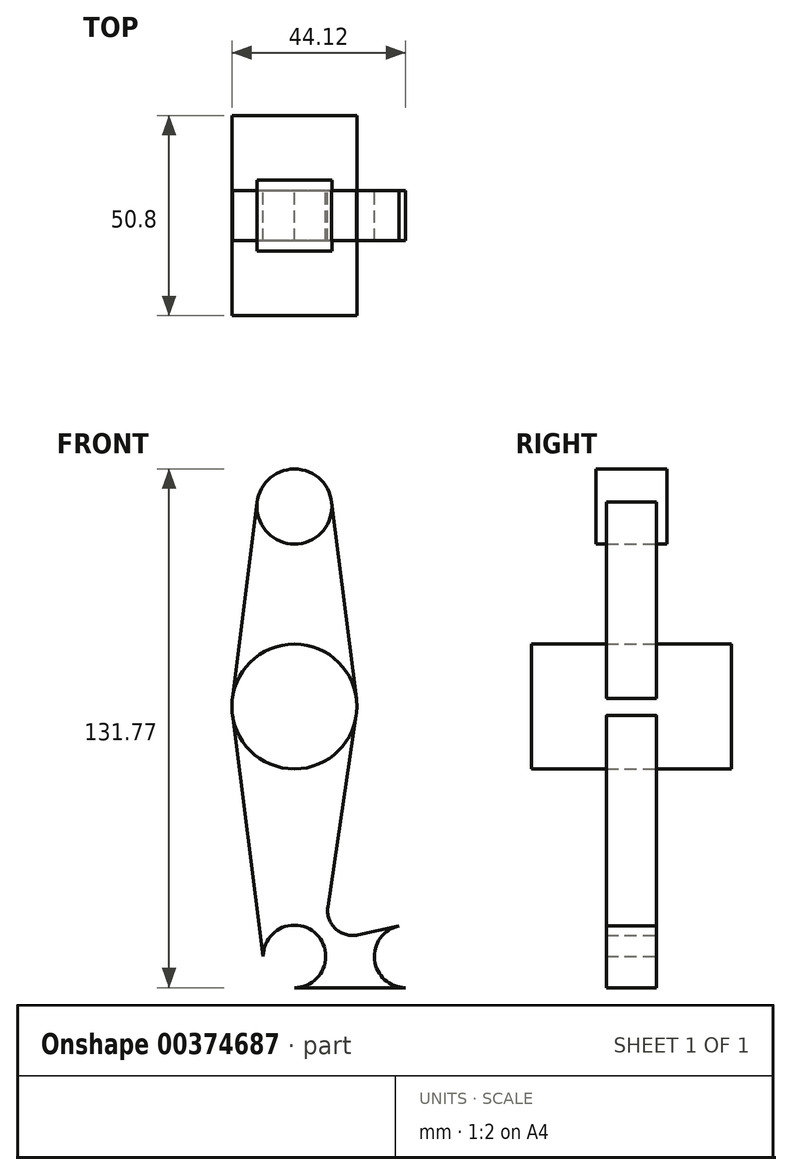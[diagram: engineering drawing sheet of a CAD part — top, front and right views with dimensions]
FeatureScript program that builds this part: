
annotation { "Feature Type Name" : "Feature", "Feature Type Description" : "" }
export const myFeature = defineFeature(function(context is Context, id is Id, definition is map)
    precondition{}
    {
        {
            var Q0;
            Q0=qCreatedBy(makeId("Front.planeOp"),FACE);
            var sketch = newSketch(context, id + "F0", { "sketchPlane" : qUnion([Q0])});
            skCircle(sketch, "E0", {"center": v(0, 0) * mm, "radius": 7.94 * mm});
            skCircle(sketch, "E1", {"center": v(0, 63.5) * mm, "radius": 15.88 * mm});
            skCircle(sketch, "E2", {"center": v(0, 114.3) * mm, "radius": 9.53 * mm});
            skCircle(sketch, "E3", {"center": v(28.24, 0) * mm, "radius": 7.94 * mm});
            skLineSegment(sketch, "E4", {"start": v(-9.45, 115.5) * mm, "end": v(-15.75, 65.48) * mm});
            skLineSegment(sketch, "E5", {"start": v(-7.94, 0) * mm, "end": v(-15.75, 61.5) * mm});
            skLineSegment(sketch, "E6", {"start": v(9.45, 115.5) * mm, "end": v(15.75, 65.48) * mm});
            skLineSegment(sketch, "E7", {"start": v(8.48, 12.6) * mm, "end": v(15.7, 61.16) * mm});
            skLineSegment(sketch, "E8", {"start": v(16.12, 5.47) * mm, "end": v(26.54, 7.75) * mm});
            skLineSegment(sketch, "E9", {"start": v(0, -7.94) * mm, "end": v(28.24, -7.94) * mm});
            skPoint(sketch, "E10.visualSharp", {"position": v(7.12, 3.5) * mm});
            skArc(sketch, "E10.filletArc", {"start": v(8.48, 12.6) * mm, "mid": v(10.42, 7.03) * mm, "end": v(16.12, 5.47) * mm});
            skLineSegment(sketch, "E11", {"start": v(-83.82, 96.93) * mm, "end": v(-83.82, 0) * mm, "construction": true});
            skSolve(sketch);
        }
        {
            var Q0;
            {var subQ0=sQuery(id+"F0.wireOp",EDGE,"E2");var subQ1=makeQuery(id+"F0.imprint","INTERSECT",VERTEX,{"derivedFrom":[subQ0,sQuery(id+"F0.wireOp",EDGE,"E4")]});Q0=makeQuery(id+"F0.imprint","IMPRINT",FACE,{"disambiguationData":[TD([[makeQuery(id+"F0.imprint","IMPRINT",EDGE,{"disambiguationData":[TD([[subQ1,1.0]])],"derivedFrom":subQ0}),1.0]])]});}
            extrude(context, id + "F1", {"entities" : qUnion([Q0]), "endBound" : BoundingType.SYMMETRIC, "depth" : 18.03 * mm});
        }
        {
            var Q0;
            {var subQ0=sQuery(id+"F0.wireOp",EDGE,"E1");var subQ1=makeQuery(id+"F0.imprint","INTERSECT",VERTEX,{"derivedFrom":[subQ0,sQuery(id+"F0.wireOp",EDGE,"E4")]});Q0=makeQuery(id+"F0.imprint","IMPRINT",FACE,{"disambiguationData":[TD([[makeQuery(id+"F0.imprint","IMPRINT",EDGE,{"disambiguationData":[TD([[subQ1,1.0]])],"derivedFrom":subQ0}),1.0]])]});}
            extrude(context, id + "F2", {"entities" : qUnion([Q0]), "endBound" : BoundingType.SYMMETRIC, "depth" : 50.8 * mm});
        }
        {
            var Q0;
            {var subQ0=sQuery(id+"F0.wireOp",EDGE,"E4");Q0=makeQuery(id+"F0.imprint","IMPRINT",FACE,{"disambiguationData":[TD([[makeQuery(id+"F0.imprint","IMPRINT",EDGE,{"derivedFrom":subQ0}),1.0]])]});}
            var Q1;
            {var subQ3=sQuery(id+"F0.wireOp",EDGE,"E5");Q1=makeQuery(id+"F0.imprint","IMPRINT",FACE,{"disambiguationData":[TD([[makeQuery(id+"F0.imprint","IMPRINT",EDGE,{"derivedFrom":subQ3}),-1.0]])]});}
            extrude(context, id + "F3", {"entities" : qUnion([Q0, Q1]), "endBound" : BoundingType.SYMMETRIC, "depth" : 12.7 * mm});
        }
    });
